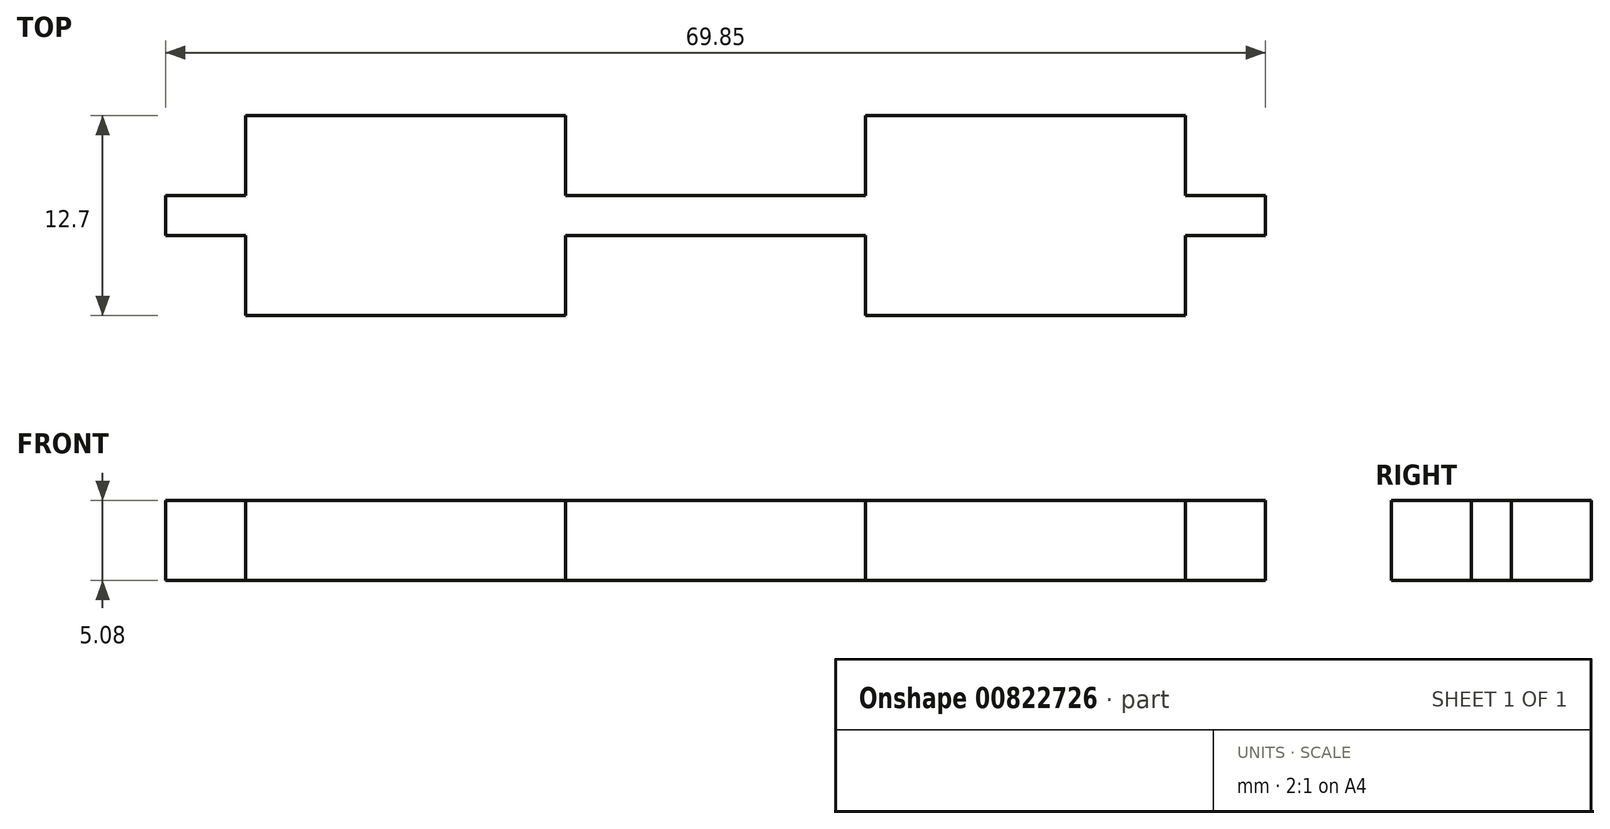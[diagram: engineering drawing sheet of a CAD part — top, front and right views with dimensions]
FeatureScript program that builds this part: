
annotation { "Feature Type Name" : "Feature", "Feature Type Description" : "" }
export const myFeature = defineFeature(function(context is Context, id is Id, definition is map)
    precondition{}
    {
        {
            var Q0;
            Q0=qCreatedBy(makeId("Top.planeOp"),FACE);
            var sketch = newSketch(context, id + "F0", { "sketchPlane" : qUnion([Q0])});
            skLineSegment(sketch, "E0.bottom", {"start": v(5.08, 0) * mm, "end": v(25.4, 0) * mm});
            skLineSegment(sketch, "E0.left", {"start": v(0, -5.08) * mm, "end": v(0, -7.62) * mm});
            skLineSegment(sketch, "E1", {"start": v(0, -5.08) * mm, "end": v(5.08, -5.08) * mm});
            skLineSegment(sketch, "E2", {"start": v(5.08, -5.08) * mm, "end": v(5.08, 0) * mm});
            skLineSegment(sketch, "E3", {"start": v(25.4, 0) * mm, "end": v(25.4, -5.08) * mm});
            skLineSegment(sketch, "E4", {"start": v(25.4, -5.08) * mm, "end": v(44.45, -5.08) * mm});
            skLineSegment(sketch, "E5", {"start": v(44.45, -5.08) * mm, "end": v(44.45, 0) * mm});
            skLineSegment(sketch, "E6", {"start": v(44.45, 0) * mm, "end": v(64.77, 0) * mm});
            skLineSegment(sketch, "E7", {"start": v(64.77, 0) * mm, "end": v(64.77, -5.08) * mm});
            skLineSegment(sketch, "E8", {"start": v(64.77, -5.08) * mm, "end": v(69.85, -5.08) * mm});
            skPoint(sketch, "E9.orphan", {"position": v(0, 0) * mm});
            skPoint(sketch, "E10.orphan", {"position": v(69.85, 0) * mm});
            skLineSegment(sketch, "E11", {"start": v(0, -7.62) * mm, "end": v(5.08, -7.62) * mm});
            skLineSegment(sketch, "E12", {"start": v(5.08, -7.62) * mm, "end": v(5.08, -12.7) * mm});
            skPoint(sketch, "E13.orphan", {"position": v(0, -12.7) * mm});
            skLineSegment(sketch, "E14", {"start": v(34.93, -5.08) * mm, "end": v(34.93, -8.66) * mm, "construction": true});
            skLineSegment(sketch, "E15.MirrorCS", {"start": v(64.77, 0) * mm, "end": v(44.45, 0) * mm});
            skLineSegment(sketch, "E16", {"start": v(0, -6.35) * mm, "end": v(3.11, -6.35) * mm, "construction": true});
            skLineSegment(sketch, "E17.MirrorCS", {"start": v(5.08, -12.7) * mm, "end": v(25.4, -12.7) * mm});
            skLineSegment(sketch, "E18.MirrorCS", {"start": v(25.4, -12.7) * mm, "end": v(25.4, -7.62) * mm});
            skLineSegment(sketch, "E19.MirrorCS", {"start": v(25.4, -7.62) * mm, "end": v(44.45, -7.62) * mm});
            skLineSegment(sketch, "E20.MirrorCS", {"start": v(44.45, -7.62) * mm, "end": v(44.45, -12.7) * mm});
            skLineSegment(sketch, "E21.MirrorCS", {"start": v(64.77, -12.7) * mm, "end": v(44.45, -12.7) * mm});
            skLineSegment(sketch, "E22.MirrorCS", {"start": v(64.77, -12.7) * mm, "end": v(64.77, -7.62) * mm});
            skLineSegment(sketch, "E23.MirrorCS", {"start": v(64.77, -7.62) * mm, "end": v(69.85, -7.62) * mm});
            skLineSegment(sketch, "E24", {"start": v(69.85, -5.08) * mm, "end": v(69.85, -7.62) * mm});
            skSolve(sketch);
        }
        {
            var Q0;
            Q0=makeQuery(id+"F0.imprint","IMPRINT",FACE,{"disambiguationData":[TD([[makeQuery(id+"F0.imprint","IMPRINT",EDGE,{"derivedFrom":sQuery(id+"F0.wireOp",EDGE,"E1")}),-1.0]])]});
            extrude(context, id + "F1", {"entities" : qUnion([Q0]), "depth" : 5.08 * mm, "offsetDistance" : 25.4 * mm});
        }
    });
